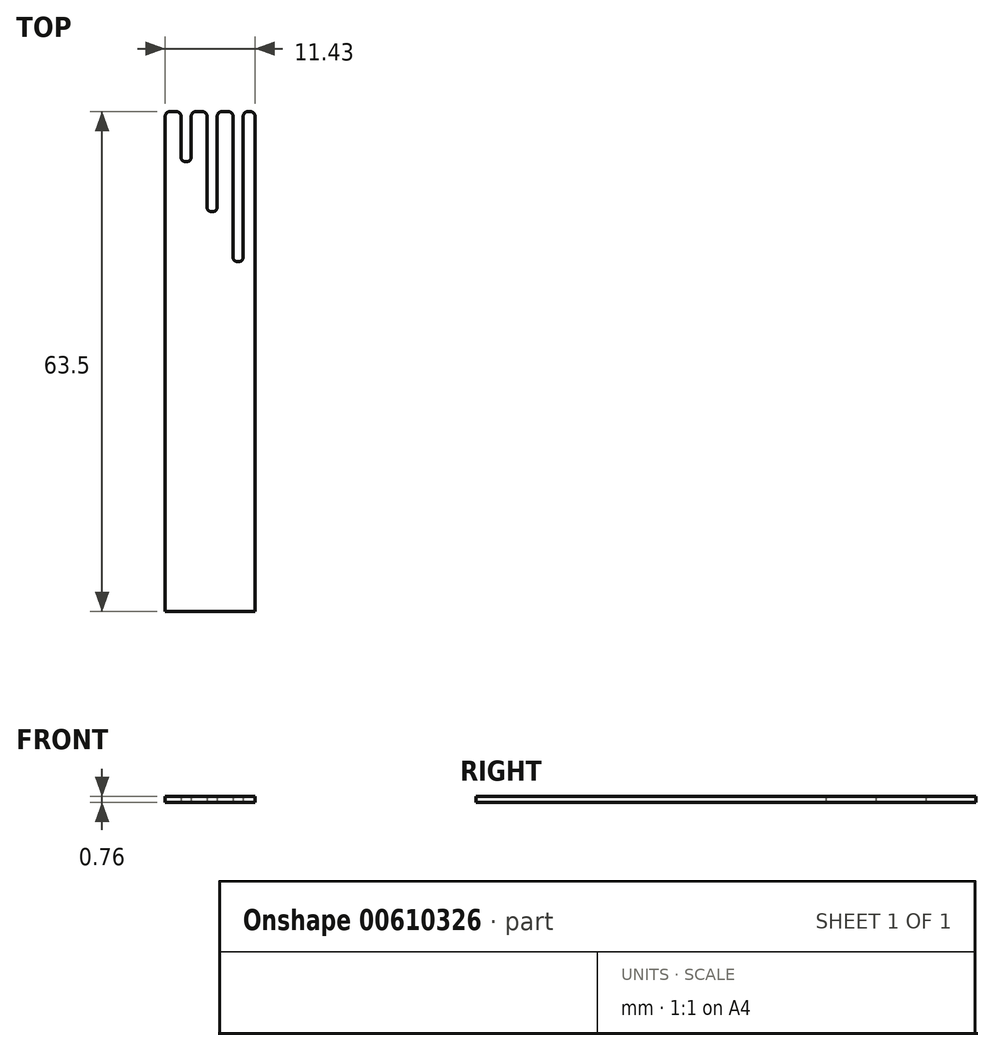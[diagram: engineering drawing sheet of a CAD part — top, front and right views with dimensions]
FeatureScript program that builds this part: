
annotation { "Feature Type Name" : "Feature", "Feature Type Description" : "" }
export const myFeature = defineFeature(function(context is Context, id is Id, definition is map)
    precondition{}
    {
        {
            var Q0;
            Q0=qCreatedBy(makeId("Top.planeOp"),FACE);
            var sketch = newSketch(context, id + "F0", { "sketchPlane" : qUnion([Q0])});
            skLineSegment(sketch, "E0.bottom", {"start": v(0, 0) * mm, "end": v(11.43, 0) * mm});
            skLineSegment(sketch, "E0.top", {"start": v(0, 63.5) * mm, "end": v(2.03, 63.5) * mm});
            skLineSegment(sketch, "E0.left", {"start": v(0, 0) * mm, "end": v(0, 63.5) * mm});
            skLineSegment(sketch, "E0.right", {"start": v(11.43, 0) * mm, "end": v(11.43, 63.5) * mm});
            skLineSegment(sketch, "E1.top", {"start": v(2.03, 57.15) * mm, "end": v(3.3, 57.15) * mm});
            skLineSegment(sketch, "E1.left", {"start": v(2.03, 63.5) * mm, "end": v(2.03, 57.15) * mm});
            skLineSegment(sketch, "E1.right", {"start": v(3.3, 63.5) * mm, "end": v(3.3, 57.15) * mm});
            skLineSegment(sketch, "E2.top", {"start": v(5.33, 50.8) * mm, "end": v(6.6, 50.8) * mm});
            skLineSegment(sketch, "E2.left", {"start": v(5.33, 63.5) * mm, "end": v(5.33, 50.8) * mm});
            skLineSegment(sketch, "E2.right", {"start": v(6.6, 63.5) * mm, "end": v(6.6, 50.8) * mm});
            skLineSegment(sketch, "E3.top", {"start": v(8.64, 44.45) * mm, "end": v(9.9, 44.45) * mm});
            skLineSegment(sketch, "E3.left", {"start": v(8.64, 63.5) * mm, "end": v(8.64, 44.45) * mm});
            skLineSegment(sketch, "E3.right", {"start": v(9.9, 63.5) * mm, "end": v(9.9, 44.45) * mm});
            skLineSegment(sketch, "E4.trimOffspring", {"start": v(3.3, 63.5) * mm, "end": v(5.33, 63.5) * mm});
            skLineSegment(sketch, "E5.trimOffspring", {"start": v(6.6, 63.5) * mm, "end": v(8.64, 63.5) * mm});
            skLineSegment(sketch, "E6.trimOffspring", {"start": v(9.9, 63.5) * mm, "end": v(11.43, 63.5) * mm});
            skSolve(sketch);
        }
        {
            var Q0;
            Q0=makeQuery(id+"F0.imprint","IMPRINT",FACE,{"disambiguationData":[TD([[makeQuery(id+"F0.imprint","IMPRINT",EDGE,{"derivedFrom":sQuery(id+"F0.wireOp",EDGE,"E0.bottom")}),1.0]])]});
            extrude(context, id + "F1", {"entities" : qUnion([Q0]), "depth" : 0.76 * mm, "offsetDistance" : 25.4 * mm});
        }
        {
            var Q0;
            Q0=makeQuery(id+"F1.opExtrude","SWEPT_EDGE",EDGE,{"disambiguationData":[OSD([sQuery(id+"F0.wireOp",EDGE,"E1.top"),sQuery(id+"F0.wireOp",EDGE,"E1.left")])]});
            var Q1;
            Q1=makeQuery(id+"F1.opExtrude","SWEPT_EDGE",EDGE,{"disambiguationData":[OSD([sQuery(id+"F0.wireOp",EDGE,"E1.top"),sQuery(id+"F0.wireOp",EDGE,"E1.right")])]});
            var Q2;
            Q2=makeQuery(id+"F1.opExtrude","SWEPT_EDGE",EDGE,{"disambiguationData":[OSD([sQuery(id+"F0.wireOp",EDGE,"E2.top"),sQuery(id+"F0.wireOp",EDGE,"E2.left")])]});
            var Q3;
            Q3=makeQuery(id+"F1.opExtrude","SWEPT_EDGE",EDGE,{"disambiguationData":[OSD([sQuery(id+"F0.wireOp",EDGE,"E2.top"),sQuery(id+"F0.wireOp",EDGE,"E2.right")])]});
            var Q4;
            Q4=makeQuery(id+"F1.opExtrude","SWEPT_EDGE",EDGE,{"disambiguationData":[OSD([sQuery(id+"F0.wireOp",EDGE,"E3.top"),sQuery(id+"F0.wireOp",EDGE,"E3.right")])]});
            var Q5;
            Q5=makeQuery(id+"F1.opExtrude","SWEPT_EDGE",EDGE,{"disambiguationData":[OSD([sQuery(id+"F0.wireOp",EDGE,"E3.top"),sQuery(id+"F0.wireOp",EDGE,"E3.left")])]});
            fillet(context, id + "F2", {"entities" : qUnion([Q0, Q1, Q2, Q3, Q4, Q5]), "radius" : 0.5 * mm, "tangentPropagation" : true, "allowEdgeOverflow" : false});
        }
        {
            var Q0;
            Q0=makeQuery(id+"F1.opExtrude","SWEPT_EDGE",EDGE,{"disambiguationData":[OSD([sQuery(id+"F0.wireOp",EDGE,"E0.top"),sQuery(id+"F0.wireOp",EDGE,"E0.left")])]});
            var Q1;
            Q1=makeQuery(id+"F1.opExtrude","SWEPT_EDGE",EDGE,{"disambiguationData":[OSD([sQuery(id+"F0.wireOp",EDGE,"E0.top"),sQuery(id+"F0.wireOp",EDGE,"E1.left")])]});
            var Q2;
            Q2=makeQuery(id+"F1.opExtrude","SWEPT_EDGE",EDGE,{"disambiguationData":[OSD([sQuery(id+"F0.wireOp",EDGE,"E1.right"),sQuery(id+"F0.wireOp",EDGE,"E4.trimOffspring")])]});
            var Q3;
            Q3=makeQuery(id+"F1.opExtrude","SWEPT_EDGE",EDGE,{"disambiguationData":[OSD([sQuery(id+"F0.wireOp",EDGE,"E2.left"),sQuery(id+"F0.wireOp",EDGE,"E4.trimOffspring")])]});
            var Q4;
            Q4=makeQuery(id+"F1.opExtrude","SWEPT_EDGE",EDGE,{"disambiguationData":[OSD([sQuery(id+"F0.wireOp",EDGE,"E2.right"),sQuery(id+"F0.wireOp",EDGE,"E5.trimOffspring")])]});
            var Q5;
            Q5=makeQuery(id+"F1.opExtrude","SWEPT_EDGE",EDGE,{"disambiguationData":[OSD([sQuery(id+"F0.wireOp",EDGE,"E3.left"),sQuery(id+"F0.wireOp",EDGE,"E5.trimOffspring")])]});
            var Q6;
            Q6=makeQuery(id+"F1.opExtrude","SWEPT_EDGE",EDGE,{"disambiguationData":[OSD([sQuery(id+"F0.wireOp",EDGE,"E3.right"),sQuery(id+"F0.wireOp",EDGE,"E6.trimOffspring")])]});
            var Q7;
            Q7=makeQuery(id+"F1.opExtrude","SWEPT_EDGE",EDGE,{"disambiguationData":[OSD([sQuery(id+"F0.wireOp",EDGE,"E0.right"),sQuery(id+"F0.wireOp",EDGE,"E6.trimOffspring")])]});
            fillet(context, id + "F3", {"entities" : qUnion([Q0, Q1, Q2, Q3, Q4, Q5, Q6, Q7]), "radius" : 0.64 * mm, "tangentPropagation" : true, "allowEdgeOverflow" : false});
        }
    });
